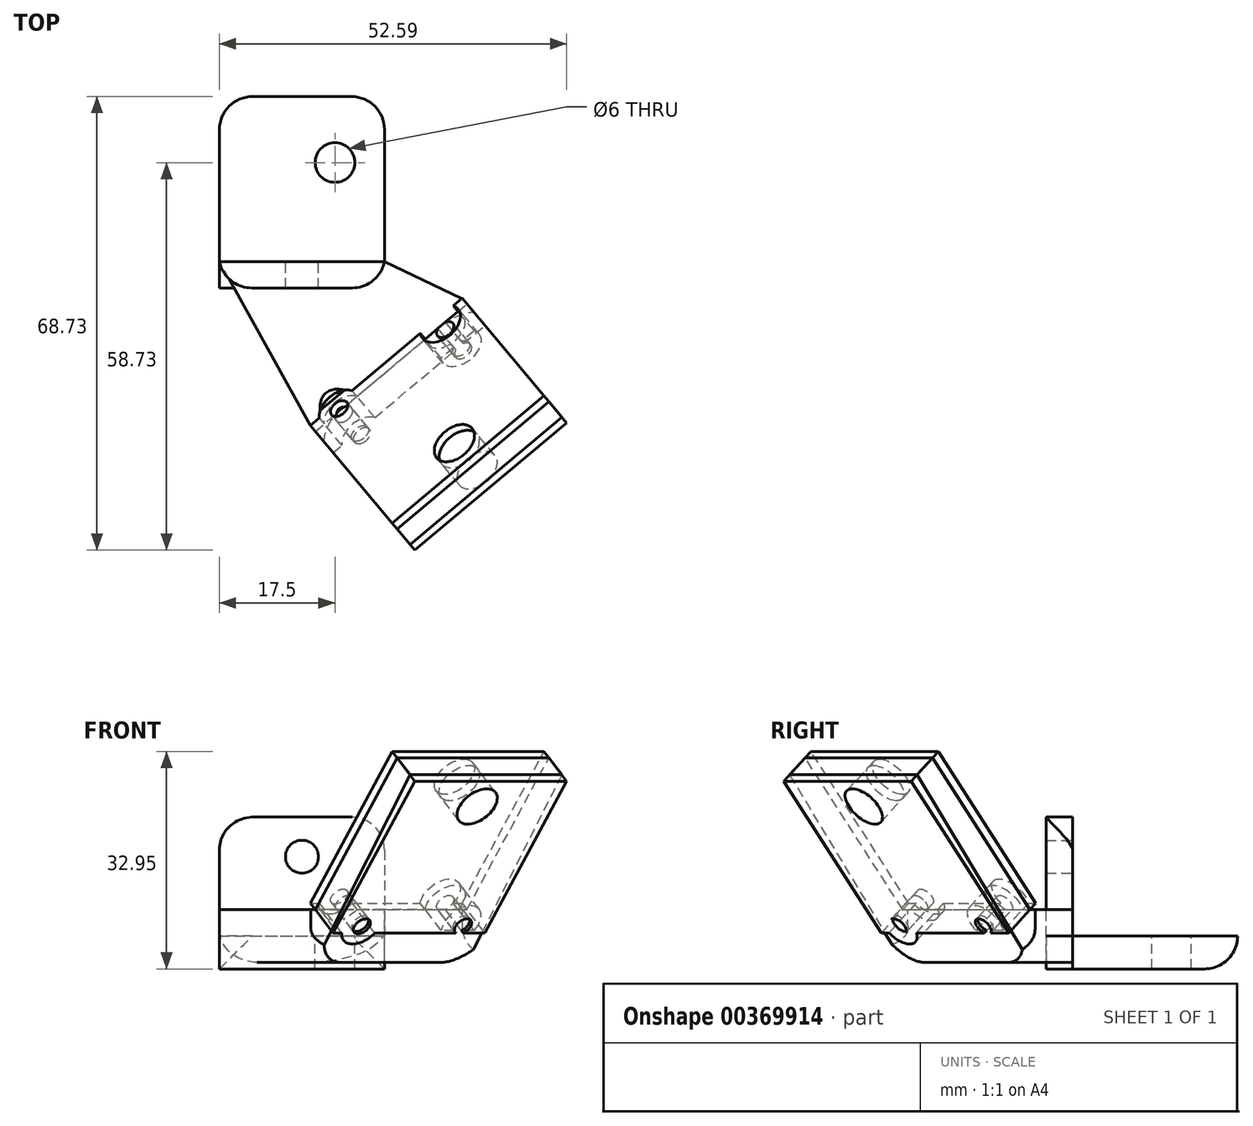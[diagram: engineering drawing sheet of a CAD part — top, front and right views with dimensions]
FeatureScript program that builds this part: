
annotation { "Feature Type Name" : "Feature", "Feature Type Description" : "" }
export const myFeature = defineFeature(function(context is Context, id is Id, definition is map)
    precondition{}
    {
        {
            var Q0;
            Q0=qCreatedBy(makeId("Top.planeOp"),FACE);
            var sketch = newSketch(context, id + "F0", { "sketchPlane" : qUnion([Q0])});
            skLineSegment(sketch, "E0.bottom", {"start": v(-12.5, 0) * mm, "end": v(12.5, 0) * mm});
            skLineSegment(sketch, "E0.top", {"start": v(-12.5, 25) * mm, "end": v(12.5, 25) * mm});
            skLineSegment(sketch, "E0.left", {"start": v(-12.5, 0) * mm, "end": v(-12.5, 25) * mm});
            skLineSegment(sketch, "E0.right", {"start": v(12.5, 0) * mm, "end": v(12.5, 25) * mm});
            skCircle(sketch, "E1", {"center": v(5, 15) * mm, "radius": 3 * mm});
            skLineSegment(sketch, "E2.top", {"start": v(-12.5, -4) * mm, "end": v(12.5, -4) * mm});
            skLineSegment(sketch, "E2.left", {"start": v(-12.5, 0) * mm, "end": v(-12.5, -4) * mm});
            skLineSegment(sketch, "E2.right", {"start": v(12.5, 0) * mm, "end": v(12.5, -4) * mm});
            skSolve(sketch);
        }
        {
            var Q0;
            Q0=makeQuery(id+"F0.imprint","IMPRINT",FACE,{"disambiguationData":[TD([[makeQuery(id+"F0.imprint","IMPRINT",EDGE,{"derivedFrom":sQuery(id+"F0.wireOp",EDGE,"E0.top")}),-1.0]])]});
            extrude(context, id + "F1", {"entities" : qUnion([Q0]), "oppositeDirection" : true, "depth" : 5 * mm});
        }
        {
            var Q0;
            Q0=makeQuery(id+"F0.imprint","IMPRINT",FACE,{"disambiguationData":[TD([[makeQuery(id+"F0.imprint","IMPRINT",EDGE,{"derivedFrom":sQuery(id+"F0.wireOp",EDGE,"E0.bottom")}),-1.0]])]});
            extrude(context, id + "F2", {"entities" : qUnion([Q0]), "depth" : 18 * mm});
        }
        {
            var Q0;
            Q0=makeQuery(id+"F2.opExtrude","CAP_FACE",FACE,{"disambiguationData":[OSD([sQuery(id+"F0.wireOp",EDGE,"E0.bottom"),sQuery(id+"F0.wireOp",EDGE,"E2.top"),sQuery(id+"F0.wireOp",EDGE,"E2.left"),sQuery(id+"F0.wireOp",EDGE,"E2.right")])],"isStart":true});
            extrude(context, id + "F3", {"entities" : qUnion([Q0]), "depth" : 5 * mm});
        }
        {
            var Q0;
            Q0=makeQuery(id+"F2.opExtrude","SWEPT_FACE",FACE,{"disambiguationData":[OSD([sQuery(id+"F0.wireOp",EDGE,"E0.bottom")])]});
            var sketch = newSketch(context, id + "F4", { "sketchPlane" : qUnion([Q0])});
            skCircle(sketch, "E3", {"center": v(0, 12) * mm, "radius": 2.5 * mm});
            skSolve(sketch);
        }
        {
            var Q0;
            Q0=makeQuery(id+"F4.imprint","IMPRINT",FACE,{"disambiguationData":[TD([[makeQuery(id+"F4.imprint","IMPRINT",EDGE,{"derivedFrom":sQuery(id+"F4.wireOp",EDGE,"E3")}),1.0]])]});
            extrude(context, id + "F5", {"entities" : qUnion([Q0]), "operationType" : NewBodyOperationType.REMOVE, "oppositeDirection" : true, "depth" : 4 * mm});
        }
        {
            var Q0;
            Q0=qCreatedBy(makeId("Top.planeOp"),FACE);
            var sketch = newSketch(context, id + "F6", { "sketchPlane" : qUnion([Q0])});
            skLineSegment(sketch, "E4", {"start": v(0, 0) * mm, "end": v(12.86, -15.32) * mm});
            skLineSegment(sketch, "E5", {"start": v(0, 0) * mm, "end": v(-12.5, 0) * mm});
            skLineSegment(sketch, "E6", {"start": v(1.37, -24.96) * mm, "end": v(12.86, -15.32) * mm});
            skLineSegment(sketch, "E7.MirrorCS", {"start": v(24.35, -5.68) * mm, "end": v(12.86, -15.32) * mm});
            skLineSegment(sketch, "E8", {"start": v(0, 0) * mm, "end": v(12.5, 0) * mm});
            skLineSegment(sketch, "E9", {"start": v(1.37, -24.96) * mm, "end": v(-12.5, 0) * mm});
            skLineSegment(sketch, "E10", {"start": v(24.35, -5.68) * mm, "end": v(12.5, 0) * mm});
            skSolve(sketch);
        }
        {
            var Q0;
            Q0=makeQuery(id+"F6.imprint","IMPRINT",FACE,{"disambiguationData":[TD([[makeQuery(id+"F6.imprint","IMPRINT",EDGE,{"derivedFrom":sQuery(id+"F6.wireOp",EDGE,"E4")}),-1.0]])]});
            var Q1;
            Q1=makeQuery(id+"F6.imprint","IMPRINT",FACE,{"disambiguationData":[TD([[makeQuery(id+"F6.imprint","IMPRINT",EDGE,{"derivedFrom":sQuery(id+"F6.wireOp",EDGE,"E4")}),1.0]])]});
            extrude(context, id + "F7", {"entities" : qUnion([Q0, Q1]), "endBound" : BoundingType.SYMMETRIC, "oppositeDirection" : true, "depth" : 8 * mm});
        }
        {
            var Q0;
            Q0=makeQuery(id+"F7.opExtrude","SWEPT_FACE",FACE,{"disambiguationData":[OSD([sQuery(id+"F6.wireOp",EDGE,"E6"),sQuery(id+"F6.wireOp",EDGE,"E7.MirrorCS")])]});
            var sketch = newSketch(context, id + "F8", { "sketchPlane" : qUnion([Q0])});
            skLineSegment(sketch, "E11.bottom", {"start": v(15, -4) * mm, "end": v(-15, -4) * mm});
            skLineSegment(sketch, "E11.top", {"start": v(15, 4) * mm, "end": v(-15, 4) * mm});
            skLineSegment(sketch, "E11.left", {"start": v(15, -4) * mm, "end": v(15, 4) * mm});
            skLineSegment(sketch, "E11.right", {"start": v(-15, -4) * mm, "end": v(-15, 4) * mm});
            skSolve(sketch);
        }
        {
            var Q0;
            Q0=makeQuery(id+"F8.imprint","IMPRINT",FACE,{"disambiguationData":[TD([[makeQuery(id+"F8.imprint","IMPRINT",EDGE,{"derivedFrom":sQuery(id+"F8.wireOp",EDGE,"E11.bottom")}),1.0]])]});
            extrude(context, id + "F9", {"entities" : qUnion([Q0]), "operationType" : NewBodyOperationType.ADD, "depth" : 1 * mm});
        }
        {
            var Q0;
            Q0=makeQuery(id+"F9.opExtrude","SWEPT_FACE",FACE,{"disambiguationData":[OSD([sQuery(id+"F8.wireOp",EDGE,"E11.left")])]});
            var sketch = newSketch(context, id + "F10", { "sketchPlane" : qUnion([Q0])});
            skLineSegment(sketch, "E12", {"start": v(-21, 4) * mm, "end": v(-40.28, 26.98) * mm});
            skLineSegment(sketch, "E13", {"start": v(-40.28, 26.98) * mm, "end": v(-43.35, 24.41) * mm});
            skLineSegment(sketch, "E14", {"start": v(-43.35, 24.41) * mm, "end": v(-21, -4) * mm});
            skSolve(sketch);
        }
        {
            var Q0;
            Q0=makeQuery(id+"F10.imprint","IMPRINT",FACE,{"disambiguationData":[TD([[makeQuery(id+"F10.imprint","IMPRINT",EDGE,{"derivedFrom":sQuery(id+"F10.wireOp",EDGE,"E12")}),1.0]])]});
            var Q1;
            Q1=makeQuery(id+"F9.opExtrude","SWEPT_FACE",FACE,{"disambiguationData":[OSD([sQuery(id+"F8.wireOp",EDGE,"E11.right")])]});
            extrude(context, id + "F11", {"entities" : qUnion([Q0]), "operationType" : NewBodyOperationType.ADD, "endBound" : BoundingType.UP_TO_SURFACE, "oppositeDirection" : true, "endBoundEntityFace" : qUnion([Q1]), "depth" : 25 * mm});
        }
        {
            var Q0;
            Q0=makeQuery(id+"F1.opExtrude","CAP_EDGE",EDGE,{"disambiguationData":[OSD([sQuery(id+"F0.wireOp",EDGE,"E0.top")])],"isStart":false});
            var Q1;
            Q1=makeQuery(id+"F2.opExtrude","SWEPT_EDGE",EDGE,{"disambiguationData":[OSD([sQuery(id+"F0.wireOp",EDGE,"E2.top"),sQuery(id+"F0.wireOp",EDGE,"E2.right")])]});
            var Q2;
            Q2=makeQuery(id+"F7.opExtrude","CAP_EDGE",EDGE,{"disambiguationData":[OSD([sQuery(id+"F6.wireOp",EDGE,"E9")])],"isStart":false});
            var Q3;
            Q3=makeQuery(id+"F7.opExtrude","CAP_EDGE",EDGE,{"disambiguationData":[OSD([sQuery(id+"F6.wireOp",EDGE,"E10")])],"isStart":false});
            var Q4;
            Q4=makeQuery(id+"F3.opExtrude","SWEPT_EDGE",EDGE,{"disambiguationData":[OSD([sQuery(id+"F0.wireOp",EDGE,"E2.top"),sQuery(id+"F0.wireOp",EDGE,"E2.right")])]});
            var Q5;
            Q5=makeQuery(id+"F2.opExtrude","CAP_EDGE",EDGE,{"disambiguationData":[OSD([sQuery(id+"F0.wireOp",EDGE,"E2.left")])],"isStart":false});
            var Q6;
            Q6=makeQuery(id+"F1.opExtrude","SWEPT_EDGE",EDGE,{"disambiguationData":[OSD([sQuery(id+"F0.wireOp",EDGE,"E0.top"),sQuery(id+"F0.wireOp",EDGE,"E0.right")])]});
            var Q7;
            Q7=makeQuery(id+"F1.opExtrude","SWEPT_EDGE",EDGE,{"disambiguationData":[OSD([sQuery(id+"F0.wireOp",EDGE,"E0.top"),sQuery(id+"F0.wireOp",EDGE,"E0.left")])]});
            var Q8;
            Q8=makeQuery(id+"F2.opExtrude","CAP_EDGE",EDGE,{"disambiguationData":[OSD([sQuery(id+"F0.wireOp",EDGE,"E2.right")])],"isStart":false});
            var Q9;
            Q9=makeQuery(id+"F2.opExtrude","SWEPT_EDGE",EDGE,{"disambiguationData":[OSD([sQuery(id+"F0.wireOp",EDGE,"E2.top"),sQuery(id+"F0.wireOp",EDGE,"E2.left")])]});
            fillet(context, id + "F12", {"entities" : qUnion([Q0, Q1, Q2, Q3, Q4, Q5, Q6, Q7, Q8, Q9]), "radius" : 5 * mm, "tangentPropagation" : true, "allowEdgeOverflow" : false});
        }
        {
            var Q0;
            Q0=makeQuery(id+"F11.opExtrude","SWEPT_FACE",FACE,{"disambiguationData":[OSD([sQuery(id+"F10.wireOp",EDGE,"E12")])]});
            var sketch = newSketch(context, id + "F13", { "sketchPlane" : qUnion([Q0])});
            skLineSegment(sketch, "E15.MirrorCS", {"start": v(22.1, -40.98) * mm, "end": v(19.73, -36.58) * mm});
            skCircle(sketch, "E16.MirrorC", {"center": v(17.28, -10.97) * mm, "radius": 3.5 * mm});
            skCircle(sketch, "E17.MirrorC", {"center": v(-0.32, -20.47) * mm, "radius": 1.5 * mm});
            skLineSegment(sketch, "E18.MirrorCS", {"start": v(8.48, -15.72) * mm, "end": v(17.28, -10.97) * mm});
            skLineSegment(sketch, "E19.MirrorCS", {"start": v(22.1, -40.98) * mm, "end": v(8.48, -15.72) * mm});
            skCircle(sketch, "E20.MirrorC", {"center": v(-0.32, -20.47) * mm, "radius": 3.5 * mm});
            skCircle(sketch, "E21.MirrorC", {"center": v(17.28, -10.97) * mm, "radius": 1.5 * mm});
            skCircle(sketch, "E22.MirrorC", {"center": v(19.73, -36.58) * mm, "radius": 1.5 * mm});
            skCircle(sketch, "E23.MirrorC", {"center": v(19.73, -36.58) * mm, "radius": 3.5 * mm});
            skLineSegment(sketch, "E24", {"start": v(22.1, -40.98) * mm, "end": v(8.9, -48.1) * mm});
            skSolve(sketch);
        }
        {
            var Q0;
            {var subQ0=sQuery(id+"F13.wireOp",EDGE,"E23.MirrorC");var subQ1=sQuery(id+"F13.wireOp",EDGE,"E19.MirrorCS");var subQ2=makeQuery(id+"F13.imprint","INTERSECT",VERTEX,{"disambiguationData":[OD(0.0)],"derivedFrom":[subQ1,subQ0]});Q0=makeQuery(id+"F13.imprint","IMPRINT",FACE,{"disambiguationData":[TD([[makeQuery(id+"F13.imprint","IMPRINT",EDGE,{"disambiguationData":[TD([[subQ2,-1.0]])],"derivedFrom":subQ1}),1.0]])]});}
            var Q1;
            {var subQ0=sQuery(id+"F13.wireOp",EDGE,"E23.MirrorC");var subQ1=sQuery(id+"F13.wireOp",EDGE,"E19.MirrorCS");var subQ2=makeQuery(id+"F13.imprint","INTERSECT",VERTEX,{"disambiguationData":[OD(0.0)],"derivedFrom":[subQ1,subQ0]});Q1=makeQuery(id+"F13.imprint","IMPRINT",FACE,{"disambiguationData":[TD([[makeQuery(id+"F13.imprint","IMPRINT",EDGE,{"disambiguationData":[TD([[subQ2,-1.0]])],"derivedFrom":subQ1}),-1.0]])]});}
            var Q2;
            {var subQ0=sQuery(id+"F13.wireOp",EDGE,"E18.MirrorCS");var subQ6=sQuery(id+"F13.wireOp",EDGE,"E21.MirrorC");var subQ7=makeQuery(id+"F13.imprint","INTERSECT",VERTEX,{"derivedFrom":[subQ0,subQ6]});Q2=makeQuery(id+"F13.imprint","IMPRINT",FACE,{"disambiguationData":[TD([[makeQuery(id+"F13.imprint","IMPRINT",EDGE,{"disambiguationData":[TD([[subQ7,1.0]])],"derivedFrom":subQ0}),-1.0]])]});}
            var Q3;
            {var subQ0=sQuery(id+"F13.wireOp",EDGE,"E16.MirrorC");var subQ1=sQuery(id+"F8.wireOp",EDGE,"E11.top");var subQ2=makeQuery(id+"F11.boolean.opBoolean","MERGE",EDGE,{"derivedFrom":[makeQuery(id+"F9.opExtrude","CAP_EDGE",EDGE,{"disambiguationData":[OSD([subQ1])],"isStart":false}),makeQuery(id+"F11.opExtrude","SWEPT_EDGE",EDGE,{"disambiguationData":[OSD([subQ1,sQuery(id+"F8.wireOp",EDGE,"E11.left"),sQuery(id+"F10.wireOp",EDGE,"E12")])]})]});var subQ3=makeQuery(id+"F13.imprint","INTERSECT",VERTEX,{"disambiguationData":[OD(0.0)],"derivedFrom":[subQ2,subQ0]});Q3=makeQuery(id+"F13.imprint","IMPRINT",FACE,{"disambiguationData":[TD([[makeQuery(id+"F13.imprint","IMPRINT",EDGE,{"disambiguationData":[TD([[subQ3,1.0]])],"derivedFrom":subQ0}),-1.0]])]});}
            var Q4;
            {var subQ0=sQuery(id+"F13.wireOp",EDGE,"E18.MirrorCS");var subQ6=sQuery(id+"F13.wireOp",EDGE,"E21.MirrorC");var subQ7=makeQuery(id+"F13.imprint","INTERSECT",VERTEX,{"derivedFrom":[subQ0,subQ6]});Q4=makeQuery(id+"F13.imprint","IMPRINT",FACE,{"disambiguationData":[TD([[makeQuery(id+"F13.imprint","IMPRINT",EDGE,{"disambiguationData":[TD([[subQ7,1.0]])],"derivedFrom":subQ0}),1.0]])]});}
            var Q5;
            {var subQ0=sQuery(id+"F13.wireOp",EDGE,"E17.MirrorC");var subQ1=sQuery(id+"F8.wireOp",EDGE,"E11.top");var subQ2=makeQuery(id+"F11.boolean.opBoolean","MERGE",EDGE,{"derivedFrom":[makeQuery(id+"F9.opExtrude","CAP_EDGE",EDGE,{"disambiguationData":[OSD([subQ1])],"isStart":false}),makeQuery(id+"F11.opExtrude","SWEPT_EDGE",EDGE,{"disambiguationData":[OSD([subQ1,sQuery(id+"F8.wireOp",EDGE,"E11.left"),sQuery(id+"F10.wireOp",EDGE,"E12")])]})]});var subQ3=makeQuery(id+"F13.imprint","INTERSECT",VERTEX,{"disambiguationData":[OD(0.0)],"derivedFrom":[subQ2,subQ0]});Q5=makeQuery(id+"F13.imprint","IMPRINT",FACE,{"disambiguationData":[TD([[makeQuery(id+"F13.imprint","IMPRINT",EDGE,{"disambiguationData":[TD([[subQ3,1.0]])],"derivedFrom":subQ0}),-1.0]])]});}
            var Q6;
            {var subQ0=sQuery(id+"F13.wireOp",EDGE,"E17.MirrorC");var subQ1=sQuery(id+"F8.wireOp",EDGE,"E11.top");var subQ2=makeQuery(id+"F11.boolean.opBoolean","MERGE",EDGE,{"derivedFrom":[makeQuery(id+"F9.opExtrude","CAP_EDGE",EDGE,{"disambiguationData":[OSD([subQ1])],"isStart":false}),makeQuery(id+"F11.opExtrude","SWEPT_EDGE",EDGE,{"disambiguationData":[OSD([subQ1,sQuery(id+"F8.wireOp",EDGE,"E11.left"),sQuery(id+"F10.wireOp",EDGE,"E12")])]})]});var subQ3=makeQuery(id+"F13.imprint","INTERSECT",VERTEX,{"disambiguationData":[OD(0.0)],"derivedFrom":[subQ2,subQ0]});Q6=makeQuery(id+"F13.imprint","IMPRINT",FACE,{"disambiguationData":[TD([[makeQuery(id+"F13.imprint","IMPRINT",EDGE,{"disambiguationData":[TD([[subQ3,-1.0]])],"derivedFrom":subQ0}),-1.0]])]});}
            extrude(context, id + "F14", {"entities" : qUnion([Q0, Q1, Q2, Q3, Q4, Q5, Q6]), "depth" : 1.5 * mm});
        }
        {
            var Q0;
            {var subQ0=sQuery(id+"F13.wireOp",EDGE,"E17.MirrorC");var subQ1=sQuery(id+"F8.wireOp",EDGE,"E11.top");var subQ2=makeQuery(id+"F11.boolean.opBoolean","MERGE",EDGE,{"derivedFrom":[makeQuery(id+"F9.opExtrude","CAP_EDGE",EDGE,{"disambiguationData":[OSD([subQ1])],"isStart":false}),makeQuery(id+"F11.opExtrude","SWEPT_EDGE",EDGE,{"disambiguationData":[OSD([subQ1,sQuery(id+"F8.wireOp",EDGE,"E11.left"),sQuery(id+"F10.wireOp",EDGE,"E12")])]})]});var subQ3=makeQuery(id+"F13.imprint","INTERSECT",VERTEX,{"disambiguationData":[OD(0.0)],"derivedFrom":[subQ2,subQ0]});Q0=makeQuery(id+"F13.imprint","IMPRINT",FACE,{"disambiguationData":[TD([[makeQuery(id+"F13.imprint","IMPRINT",EDGE,{"disambiguationData":[TD([[subQ3,-1.0]])],"derivedFrom":subQ0}),1.0]])]});}
            var Q1;
            {var subQ0=sQuery(id+"F13.wireOp",EDGE,"E17.MirrorC");var subQ1=sQuery(id+"F8.wireOp",EDGE,"E11.top");var subQ2=makeQuery(id+"F11.boolean.opBoolean","MERGE",EDGE,{"derivedFrom":[makeQuery(id+"F9.opExtrude","CAP_EDGE",EDGE,{"disambiguationData":[OSD([subQ1])],"isStart":false}),makeQuery(id+"F11.opExtrude","SWEPT_EDGE",EDGE,{"disambiguationData":[OSD([subQ1,sQuery(id+"F8.wireOp",EDGE,"E11.left"),sQuery(id+"F10.wireOp",EDGE,"E12")])]})]});var subQ3=makeQuery(id+"F13.imprint","INTERSECT",VERTEX,{"disambiguationData":[OD(0.0)],"derivedFrom":[subQ2,subQ0]});Q1=makeQuery(id+"F13.imprint","IMPRINT",FACE,{"disambiguationData":[TD([[makeQuery(id+"F13.imprint","IMPRINT",EDGE,{"disambiguationData":[TD([[subQ3,1.0]])],"derivedFrom":subQ0}),1.0]])]});}
            var Q2;
            {var subQ0=sQuery(id+"F13.wireOp",EDGE,"E21.MirrorC");var subQ1=makeQuery(id+"F13.imprint","INTERSECT",VERTEX,{"derivedFrom":[sQuery(id+"F13.wireOp",EDGE,"E18.MirrorCS"),subQ0]});Q2=makeQuery(id+"F13.imprint","IMPRINT",FACE,{"disambiguationData":[TD([[makeQuery(id+"F13.imprint","IMPRINT",EDGE,{"disambiguationData":[TD([[subQ1,-1.0]])],"derivedFrom":subQ0}),-1.0]])]});}
            var Q3;
            {var subQ0=sQuery(id+"F13.wireOp",EDGE,"E21.MirrorC");var subQ1=sQuery(id+"F8.wireOp",EDGE,"E11.top");var subQ2=makeQuery(id+"F11.boolean.opBoolean","MERGE",EDGE,{"derivedFrom":[makeQuery(id+"F9.opExtrude","CAP_EDGE",EDGE,{"disambiguationData":[OSD([subQ1])],"isStart":false}),makeQuery(id+"F11.opExtrude","SWEPT_EDGE",EDGE,{"disambiguationData":[OSD([subQ1,sQuery(id+"F8.wireOp",EDGE,"E11.left"),sQuery(id+"F10.wireOp",EDGE,"E12")])]})]});var subQ3=makeQuery(id+"F13.imprint","INTERSECT",VERTEX,{"disambiguationData":[OD(0.0)],"derivedFrom":[subQ2,subQ0]});Q3=makeQuery(id+"F13.imprint","IMPRINT",FACE,{"disambiguationData":[TD([[makeQuery(id+"F13.imprint","IMPRINT",EDGE,{"disambiguationData":[TD([[subQ3,-1.0]])],"derivedFrom":subQ0}),-1.0]])]});}
            var Q4;
            {var subQ0=sQuery(id+"F13.wireOp",EDGE,"E19.MirrorCS");var subQ1=makeQuery(id+"F13.imprint","IMPRINT",VERTEX,{"derivedFrom":subQ0});Q4=makeQuery(id+"F13.imprint","IMPRINT",FACE,{"disambiguationData":[TD([[makeQuery(id+"F13.imprint","IMPRINT",EDGE,{"disambiguationData":[TD([[subQ1,1.0]])],"derivedFrom":subQ0}),-1.0]])]});}
            var Q5;
            {var subQ0=sQuery(id+"F13.wireOp",EDGE,"E19.MirrorCS");var subQ1=makeQuery(id+"F13.imprint","IMPRINT",VERTEX,{"derivedFrom":subQ0});Q5=makeQuery(id+"F13.imprint","IMPRINT",FACE,{"disambiguationData":[TD([[makeQuery(id+"F13.imprint","IMPRINT",EDGE,{"disambiguationData":[TD([[subQ1,1.0]])],"derivedFrom":subQ0}),1.0]])]});}
            extrude(context, id + "F15", {"entities" : qUnion([Q0, Q1, Q2, Q3, Q4, Q5]), "operationType" : NewBodyOperationType.REMOVE, "endBound" : BoundingType.SYMMETRIC, "oppositeDirection" : true, "depth" : 20 * mm});
        }
        {
            var Q0;
            Q0=makeQuery(id+"F14.opExtrude","CAP_FACE",FACE,{"disambiguationData":[OSD([sQuery(id+"F13.wireOp",EDGE,"E17.MirrorC"),sQuery(id+"F13.wireOp",EDGE,"E20.MirrorC")])],"isStart":false});
            var Q1;
            Q1=makeQuery(id+"F14.opExtrude","CAP_FACE",FACE,{"disambiguationData":[OSD([sQuery(id+"F13.wireOp",EDGE,"E22.MirrorC"),sQuery(id+"F13.wireOp",EDGE,"E23.MirrorC")])],"isStart":false});
            var Q2;
            Q2=makeQuery(id+"F14.opExtrude","CAP_FACE",FACE,{"disambiguationData":[OSD([sQuery(id+"F13.wireOp",EDGE,"E16.MirrorC"),sQuery(id+"F13.wireOp",EDGE,"E21.MirrorC")])],"isStart":false});
            extrude(context, id + "F16", {"entities" : qUnion([Q0, Q1, Q2]), "operationType" : NewBodyOperationType.REMOVE, "depth" : 10 * mm});
        }
        {
            var Q0;
            {var subQ0=sQuery(id+"F13.wireOp",EDGE,"E23.MirrorC");var subQ1=sQuery(id+"F13.wireOp",EDGE,"E19.MirrorCS");var subQ2=makeQuery(id+"F13.imprint","INTERSECT",VERTEX,{"disambiguationData":[OD(0.0)],"derivedFrom":[subQ1,subQ0]});Q0=makeQuery(id+"F13.imprint","IMPRINT",FACE,{"disambiguationData":[TD([[makeQuery(id+"F13.imprint","IMPRINT",EDGE,{"disambiguationData":[TD([[subQ2,-1.0]])],"derivedFrom":subQ1}),1.0]])]});}
            var Q1;
            {var subQ0=sQuery(id+"F13.wireOp",EDGE,"E23.MirrorC");var subQ1=sQuery(id+"F13.wireOp",EDGE,"E19.MirrorCS");var subQ2=makeQuery(id+"F13.imprint","INTERSECT",VERTEX,{"disambiguationData":[OD(0.0)],"derivedFrom":[subQ1,subQ0]});Q1=makeQuery(id+"F13.imprint","IMPRINT",FACE,{"disambiguationData":[TD([[makeQuery(id+"F13.imprint","IMPRINT",EDGE,{"disambiguationData":[TD([[subQ2,-1.0]])],"derivedFrom":subQ1}),-1.0]])]});}
            var Q2;
            {var subQ0=sQuery(id+"F13.wireOp",EDGE,"E17.MirrorC");var subQ1=sQuery(id+"F8.wireOp",EDGE,"E11.top");var subQ2=makeQuery(id+"F11.boolean.opBoolean","MERGE",EDGE,{"derivedFrom":[makeQuery(id+"F9.opExtrude","CAP_EDGE",EDGE,{"disambiguationData":[OSD([subQ1])],"isStart":false}),makeQuery(id+"F11.opExtrude","SWEPT_EDGE",EDGE,{"disambiguationData":[OSD([subQ1,sQuery(id+"F8.wireOp",EDGE,"E11.left"),sQuery(id+"F10.wireOp",EDGE,"E12")])]})]});var subQ3=makeQuery(id+"F13.imprint","INTERSECT",VERTEX,{"disambiguationData":[OD(0.0)],"derivedFrom":[subQ2,subQ0]});Q2=makeQuery(id+"F13.imprint","IMPRINT",FACE,{"disambiguationData":[TD([[makeQuery(id+"F13.imprint","IMPRINT",EDGE,{"disambiguationData":[TD([[subQ3,1.0]])],"derivedFrom":subQ0}),-1.0]])]});}
            var Q3;
            {var subQ0=sQuery(id+"F13.wireOp",EDGE,"E17.MirrorC");var subQ1=sQuery(id+"F8.wireOp",EDGE,"E11.top");var subQ2=makeQuery(id+"F11.boolean.opBoolean","MERGE",EDGE,{"derivedFrom":[makeQuery(id+"F9.opExtrude","CAP_EDGE",EDGE,{"disambiguationData":[OSD([subQ1])],"isStart":false}),makeQuery(id+"F11.opExtrude","SWEPT_EDGE",EDGE,{"disambiguationData":[OSD([subQ1,sQuery(id+"F8.wireOp",EDGE,"E11.left"),sQuery(id+"F10.wireOp",EDGE,"E12")])]})]});var subQ3=makeQuery(id+"F13.imprint","INTERSECT",VERTEX,{"disambiguationData":[OD(0.0)],"derivedFrom":[subQ2,subQ0]});Q3=makeQuery(id+"F13.imprint","IMPRINT",FACE,{"disambiguationData":[TD([[makeQuery(id+"F13.imprint","IMPRINT",EDGE,{"disambiguationData":[TD([[subQ3,-1.0]])],"derivedFrom":subQ0}),-1.0]])]});}
            var Q4;
            {var subQ0=sQuery(id+"F13.wireOp",EDGE,"E16.MirrorC");var subQ1=sQuery(id+"F8.wireOp",EDGE,"E11.top");var subQ2=makeQuery(id+"F11.boolean.opBoolean","MERGE",EDGE,{"derivedFrom":[makeQuery(id+"F9.opExtrude","CAP_EDGE",EDGE,{"disambiguationData":[OSD([subQ1])],"isStart":false}),makeQuery(id+"F11.opExtrude","SWEPT_EDGE",EDGE,{"disambiguationData":[OSD([subQ1,sQuery(id+"F8.wireOp",EDGE,"E11.left"),sQuery(id+"F10.wireOp",EDGE,"E12")])]})]});var subQ3=makeQuery(id+"F13.imprint","INTERSECT",VERTEX,{"disambiguationData":[OD(0.0)],"derivedFrom":[subQ2,subQ0]});Q4=makeQuery(id+"F13.imprint","IMPRINT",FACE,{"disambiguationData":[TD([[makeQuery(id+"F13.imprint","IMPRINT",EDGE,{"disambiguationData":[TD([[subQ3,1.0]])],"derivedFrom":subQ0}),-1.0]])]});}
            var Q5;
            {var subQ0=sQuery(id+"F13.wireOp",EDGE,"E18.MirrorCS");var subQ6=sQuery(id+"F13.wireOp",EDGE,"E21.MirrorC");var subQ7=makeQuery(id+"F13.imprint","INTERSECT",VERTEX,{"derivedFrom":[subQ0,subQ6]});Q5=makeQuery(id+"F13.imprint","IMPRINT",FACE,{"disambiguationData":[TD([[makeQuery(id+"F13.imprint","IMPRINT",EDGE,{"disambiguationData":[TD([[subQ7,1.0]])],"derivedFrom":subQ0}),-1.0]])]});}
            var Q6;
            {var subQ0=sQuery(id+"F13.wireOp",EDGE,"E18.MirrorCS");var subQ6=sQuery(id+"F13.wireOp",EDGE,"E21.MirrorC");var subQ7=makeQuery(id+"F13.imprint","INTERSECT",VERTEX,{"derivedFrom":[subQ0,subQ6]});Q6=makeQuery(id+"F13.imprint","IMPRINT",FACE,{"disambiguationData":[TD([[makeQuery(id+"F13.imprint","IMPRINT",EDGE,{"disambiguationData":[TD([[subQ7,1.0]])],"derivedFrom":subQ0}),1.0]])]});}
            extrude(context, id + "F17", {"entities" : qUnion([Q0, Q1, Q2, Q3, Q4, Q5, Q6]), "oppositeDirection" : true, "depth" : 5.5 * mm});
        }
    });
